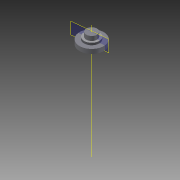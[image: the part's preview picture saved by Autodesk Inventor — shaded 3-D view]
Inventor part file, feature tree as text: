
AUTODESK INVENTOR PART (.ipt)
format: ipt  version: 2012 (Build 160160000, 160)  size: 1,805,312 bytes
history: native  units: mm
features: sketch x7, other x4, extrude x4, projected_geometry x2, plane x1
ambient origin geometry x8: Origin, YZ Plane, XZ Plane, XY Plane, X Axis, Y Axis, Z Axis, Center Point
bodies: Solid1 (feature_tree)
feature tree (18):
  other  "Gear2_LargeAndSmall.iam"
  other  "Spur Gear2:1"
  other  "Spur Gear1:1"
  sketch  "Sketch2"  dims[d0=10.0mm d1=3.3mm]
  sketch  "Sketch3"  dims[d2=10.0mm d3=0.0mm d4=22.5mm]
  other  "Work Axis1"
  extrude  "Extrusion1"  Depth=3.3mm
  sketch  "Sketch5"  dims[d8=10.0mm d9=0.0mm d11=10.0mm d12=0.0mm]
  plane  "Work Plane1"
  extrude  "Extrusion2"  Depth=22.5mm
  extrude  "Extrusion3"  Depth=15.909903mm
  extrude  "Extrusion4"  Depth=10.0mm TaperAngle=0.0deg
  projected_geometry  "Projected Loop1"
  projected_geometry  "Projected Loop2"
  sketch  "Sketch4"  dims[d5=10.0mm d6=0.0mm d7=15.909903mm]
  sketch  "Sketch6"
  sketch  "Sketch7"
  sketch  "Sketch8"
